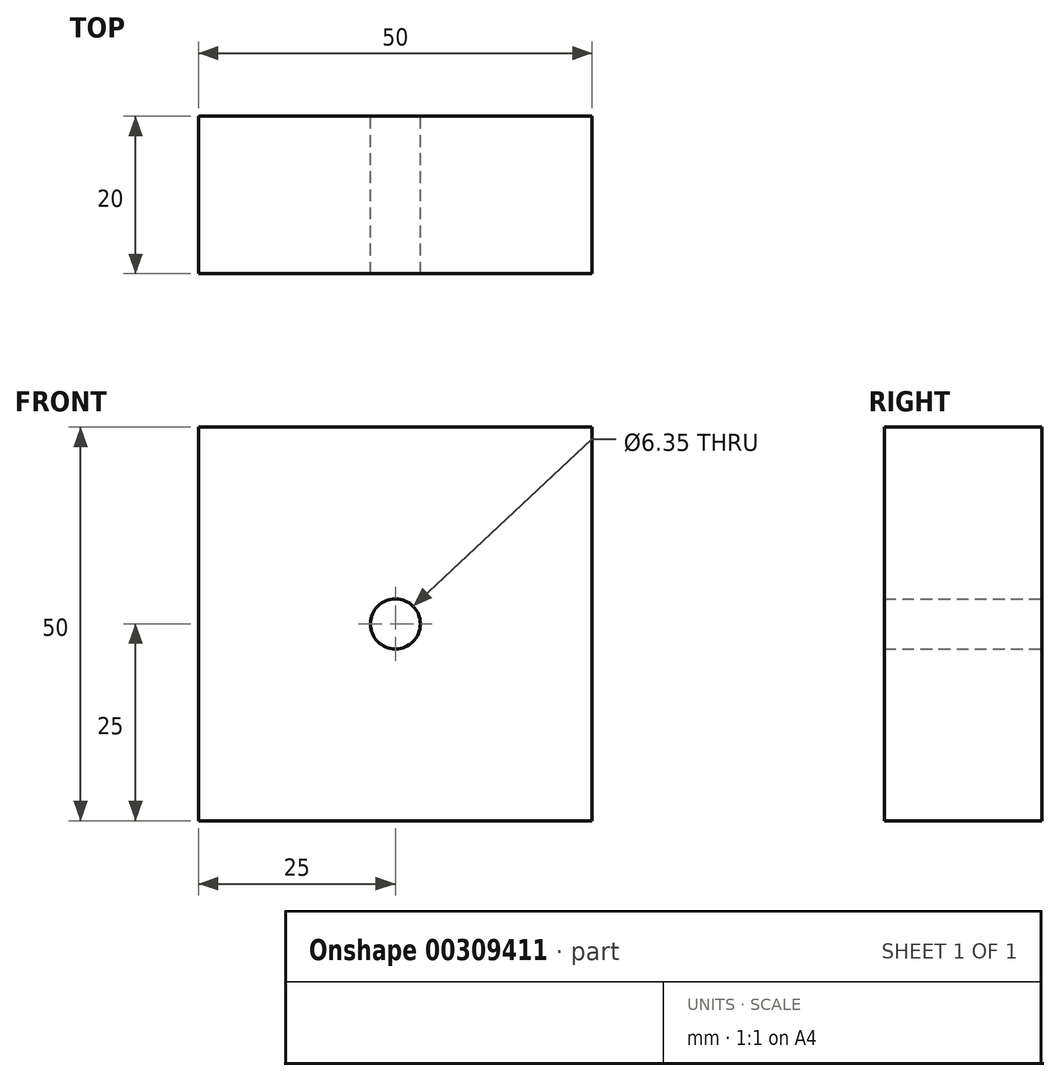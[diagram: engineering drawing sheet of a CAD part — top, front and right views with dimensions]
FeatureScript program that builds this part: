
annotation { "Feature Type Name" : "Feature", "Feature Type Description" : "" }
export const myFeature = defineFeature(function(context is Context, id is Id, definition is map)
    precondition{}
    {
        {
            var Q0;
            Q0=qCreatedBy(makeId("Front.planeOp"),FACE);
            var sketch = newSketch(context, id + "F0", { "sketchPlane" : qUnion([Q0])});
            skLineSegment(sketch, "E0.bottom", {"start": v(25, -25) * mm, "end": v(-25, -25) * mm});
            skLineSegment(sketch, "E0.top", {"start": v(25, 25) * mm, "end": v(-25, 25) * mm});
            skLineSegment(sketch, "E0.left", {"start": v(25, -25) * mm, "end": v(25, 25) * mm});
            skLineSegment(sketch, "E0.right", {"start": v(-25, -25) * mm, "end": v(-25, 25) * mm});
            skPoint(sketch, "E0.middle", {"position": v(0, 0) * mm});
            skCircle(sketch, "E1", {"center": v(0, 0) * mm, "radius": 3.18 * mm});
            skSolve(sketch);
        }
        {
            var Q0;
            Q0 = qSketchRegion(id + "F0", true);
            extrude(context, id + "F1", {"entities" : qUnion([Q0]), "depth" : 20 * mm});
        }
    });
